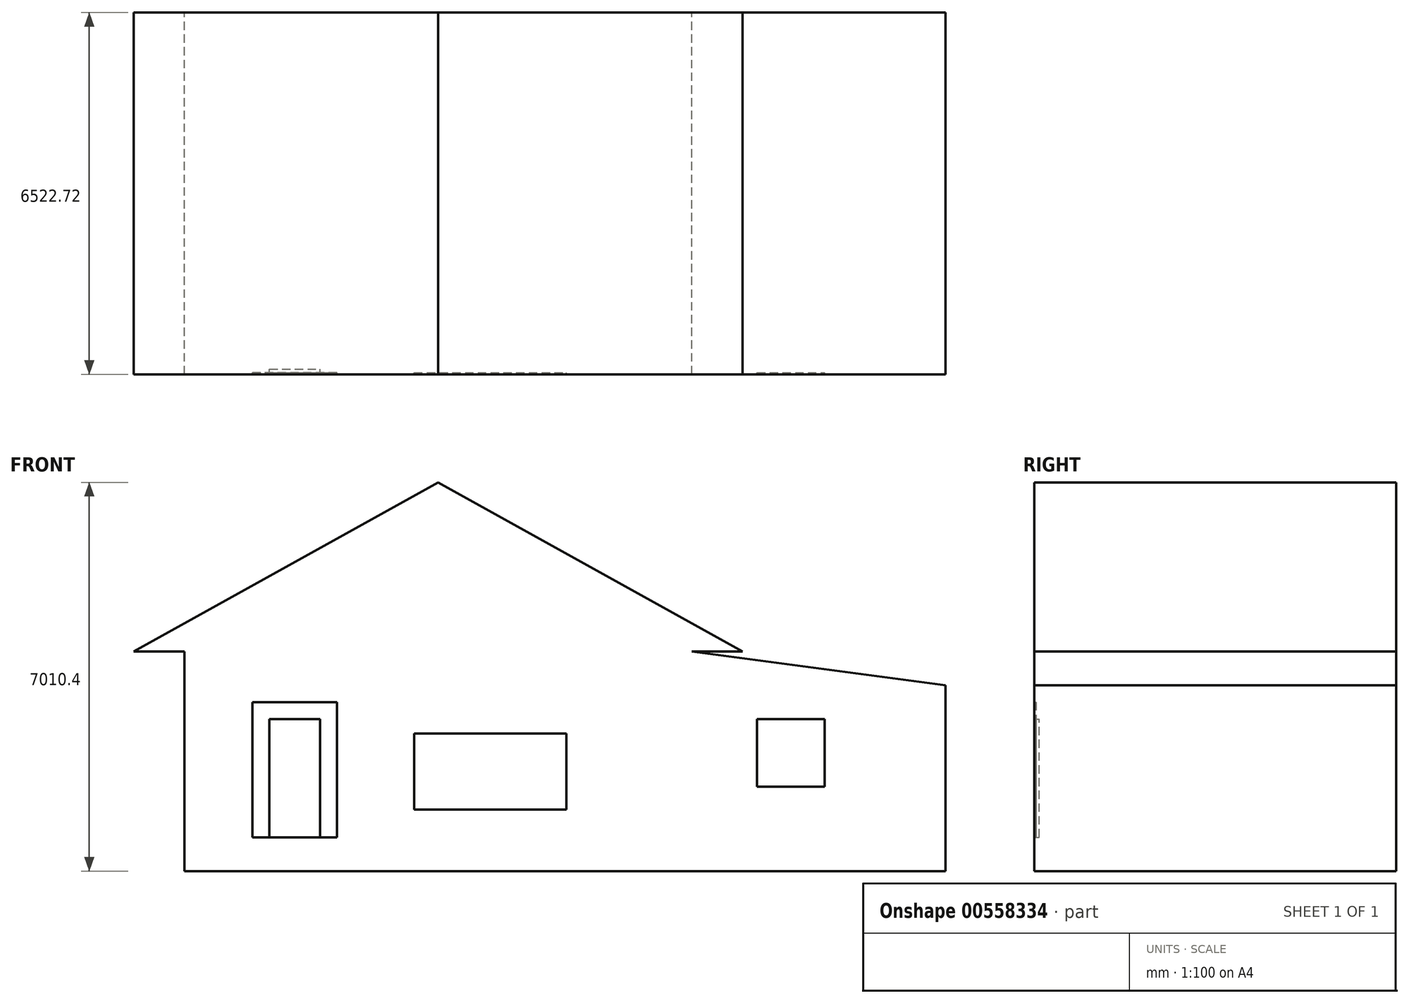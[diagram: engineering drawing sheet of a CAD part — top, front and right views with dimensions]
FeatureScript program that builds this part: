
annotation { "Feature Type Name" : "Feature", "Feature Type Description" : "" }
export const myFeature = defineFeature(function(context is Context, id is Id, definition is map)
    precondition{}
    {
        {
            var Q0;
            Q0=qCreatedBy(makeId("Front.planeOp"),FACE);
            var sketch = newSketch(context, id + "F0", { "sketchPlane" : qUnion([Q0])});
            skLineSegment(sketch, "E0", {"start": v(-24792.4, -8254.81) * mm, "end": v(-15648.4, -8254.81) * mm});
            skLineSegment(sketch, "E1", {"start": v(-24792.4, -8254.81) * mm, "end": v(-24792.4, -7645.21) * mm});
            skLineSegment(sketch, "E2", {"start": v(-24792.4, -7645.21) * mm, "end": v(-15648.4, -7645.21) * mm});
            skLineSegment(sketch, "E3", {"start": v(-15648.4, -7645.21) * mm, "end": v(-15648.4, -8254.81) * mm});
            skLineSegment(sketch, "E4", {"start": v(-15648.4, -8254.81) * mm, "end": v(-11076.4, -8254.81) * mm});
            skLineSegment(sketch, "E5", {"start": v(-11076.4, -8254.81) * mm, "end": v(-11076.4, -7645.21) * mm});
            skLineSegment(sketch, "E6", {"start": v(-11076.4, -7645.21) * mm, "end": v(-15648.4, -7645.21) * mm});
            skLineSegment(sketch, "E7", {"start": v(-24792.4, -7645.21) * mm, "end": v(-24792.4, -4292.41) * mm});
            skLineSegment(sketch, "E8", {"start": v(-15648.4, -7645.21) * mm, "end": v(-15648.4, -4292.41) * mm});
            skLineSegment(sketch, "E9", {"start": v(-24792.4, -4292.41) * mm, "end": v(-15648.4, -4292.41) * mm});
            skLineSegment(sketch, "E10", {"start": v(-24792.4, -4292.41) * mm, "end": v(-25706.8, -4292.41) * mm});
            skLineSegment(sketch, "E11", {"start": v(-15648.4, -4292.41) * mm, "end": v(-14734, -4292.41) * mm});
            skLineSegment(sketch, "E12", {"start": v(-20220.4, -4292.41) * mm, "end": v(-20220.4, -2006.41) * mm});
            skLineSegment(sketch, "E13", {"start": v(-20220.4, -2006.41) * mm, "end": v(-24792.4, -4292.41) * mm});
            skLineSegment(sketch, "E14", {"start": v(-20220.4, -2006.41) * mm, "end": v(-15648.4, -4292.41) * mm});
            skLineSegment(sketch, "E15", {"start": v(-20220.4, -2006.41) * mm, "end": v(-20220.4, -1244.41) * mm});
            skLineSegment(sketch, "E16", {"start": v(-20220.4, -1244.41) * mm, "end": v(-25706.8, -4292.41) * mm});
            skLineSegment(sketch, "E17", {"start": v(-20220.4, -1244.41) * mm, "end": v(-14734, -4292.41) * mm});
            skLineSegment(sketch, "E18", {"start": v(-11076.4, -7645.21) * mm, "end": v(-11076.4, -4902.01) * mm});
            skLineSegment(sketch, "E19", {"start": v(-15648.4, -4292.41) * mm, "end": v(-11076.4, -4902.01) * mm});
            skLineSegment(sketch, "E20", {"start": v(-11076.4, -5601.2) * mm, "end": v(-15648.4, -4902.01) * mm});
            skLineSegment(sketch, "E21", {"start": v(-23263.22, -7645.21) * mm, "end": v(-23263.22, -5511.61) * mm});
            skLineSegment(sketch, "E22", {"start": v(-23263.22, -5511.61) * mm, "end": v(-22348.82, -5511.61) * mm});
            skLineSegment(sketch, "E23", {"start": v(-22348.82, -5511.61) * mm, "end": v(-22348.82, -7645.21) * mm});
            skLineSegment(sketch, "E24", {"start": v(-22348.82, -7645.21) * mm, "end": v(-22044.02, -7645.21) * mm});
            skLineSegment(sketch, "E25", {"start": v(-22044.02, -7645.21) * mm, "end": v(-22044.02, -5511.61) * mm});
            skLineSegment(sketch, "E26", {"start": v(-22044.02, -5511.61) * mm, "end": v(-22044.02, -5206.81) * mm});
            skLineSegment(sketch, "E27", {"start": v(-23263.22, -7645.21) * mm, "end": v(-23568.02, -7645.21) * mm});
            skLineSegment(sketch, "E28", {"start": v(-22044.02, -5206.81) * mm, "end": v(-23263.22, -5206.81) * mm});
            skLineSegment(sketch, "E29", {"start": v(-23263.22, -5206.81) * mm, "end": v(-23568.02, -5206.81) * mm});
            skLineSegment(sketch, "E30", {"start": v(-23568.02, -5206.81) * mm, "end": v(-23568.02, -7645.21) * mm});
            skPoint(sketch, "E31.endSnap0", {"position": v(-15648.4, -5968.81) * mm});
            skLineSegment(sketch, "E32", {"start": v(-20654.73, -5776.06) * mm, "end": v(-20654.73, -7147.66) * mm});
            skLineSegment(sketch, "E33", {"start": v(-20654.73, -5776.06) * mm, "end": v(-17911.53, -5776.06) * mm});
            skLineSegment(sketch, "E34", {"start": v(-17911.53, -5776.06) * mm, "end": v(-17911.53, -7147.66) * mm});
            skLineSegment(sketch, "E35", {"start": v(-17911.53, -7147.66) * mm, "end": v(-20654.73, -7147.66) * mm});
            skLineSegment(sketch, "E36", {"start": v(-14474.71, -5511.61) * mm, "end": v(-13255.51, -5511.61) * mm});
            skLineSegment(sketch, "E37", {"start": v(-13255.51, -5511.61) * mm, "end": v(-13255.51, -6730.81) * mm});
            skLineSegment(sketch, "E38", {"start": v(-13255.51, -6730.81) * mm, "end": v(-14474.71, -6730.81) * mm});
            skLineSegment(sketch, "E39", {"start": v(-14474.71, -5511.61) * mm, "end": v(-14474.71, -6730.81) * mm});
            skSolve(sketch);
        }
        {
            var Q0;
            Q0 = qSketchRegion(id + "F0", true);
            extrude(context, id + "F1", {"entities" : qUnion([Q0]), "depth" : 6522.72 * mm, "offsetDistance" : 30.48 * mm});
        }
        {
            var Q0;
            {var subQ0=sQuery(id+"F0.wireOp",EDGE,"E21");Q0=makeQuery(id+"F0.imprint","IMPRINT",FACE,{"disambiguationData":[TD([[makeQuery(id+"F0.imprint","IMPRINT",EDGE,{"derivedFrom":subQ0}),-1.0]])]});}
            extrude(context, id + "F2", {"entities" : qUnion([Q0]), "operationType" : NewBodyOperationType.ADD, "depth" : 6431.28 * mm, "offsetDistance" : 30.48 * mm});
        }
        {
            var Q0;
            Q0=makeQuery(id+"F0.imprint","IMPRINT",FACE,{"disambiguationData":[TD([[makeQuery(id+"F0.imprint","IMPRINT",EDGE,{"derivedFrom":sQuery(id+"F0.wireOp",EDGE,"E21")}),1.0]])]});
            extrude(context, id + "F3", {"entities" : qUnion([Q0]), "operationType" : NewBodyOperationType.ADD, "depth" : 6492.24 * mm, "offsetDistance" : 30.48 * mm});
        }
        {
            var Q0;
            Q0=makeQuery(id+"F0.imprint","IMPRINT",FACE,{"disambiguationData":[TD([[makeQuery(id+"F0.imprint","IMPRINT",EDGE,{"derivedFrom":sQuery(id+"F0.wireOp",EDGE,"E32")}),1.0]])]});
            extrude(context, id + "F4", {"entities" : qUnion([Q0]), "operationType" : NewBodyOperationType.ADD, "depth" : 6492.24 * mm, "offsetDistance" : 30.48 * mm});
        }
        {
            var Q0;
            Q0=makeQuery(id+"F0.imprint","IMPRINT",FACE,{"disambiguationData":[TD([[makeQuery(id+"F0.imprint","IMPRINT",EDGE,{"derivedFrom":sQuery(id+"F0.wireOp",EDGE,"E36")}),-1.0]])]});
            extrude(context, id + "F5", {"entities" : qUnion([Q0]), "operationType" : NewBodyOperationType.ADD, "depth" : 6492.24 * mm, "offsetDistance" : 30.48 * mm});
        }
    });
